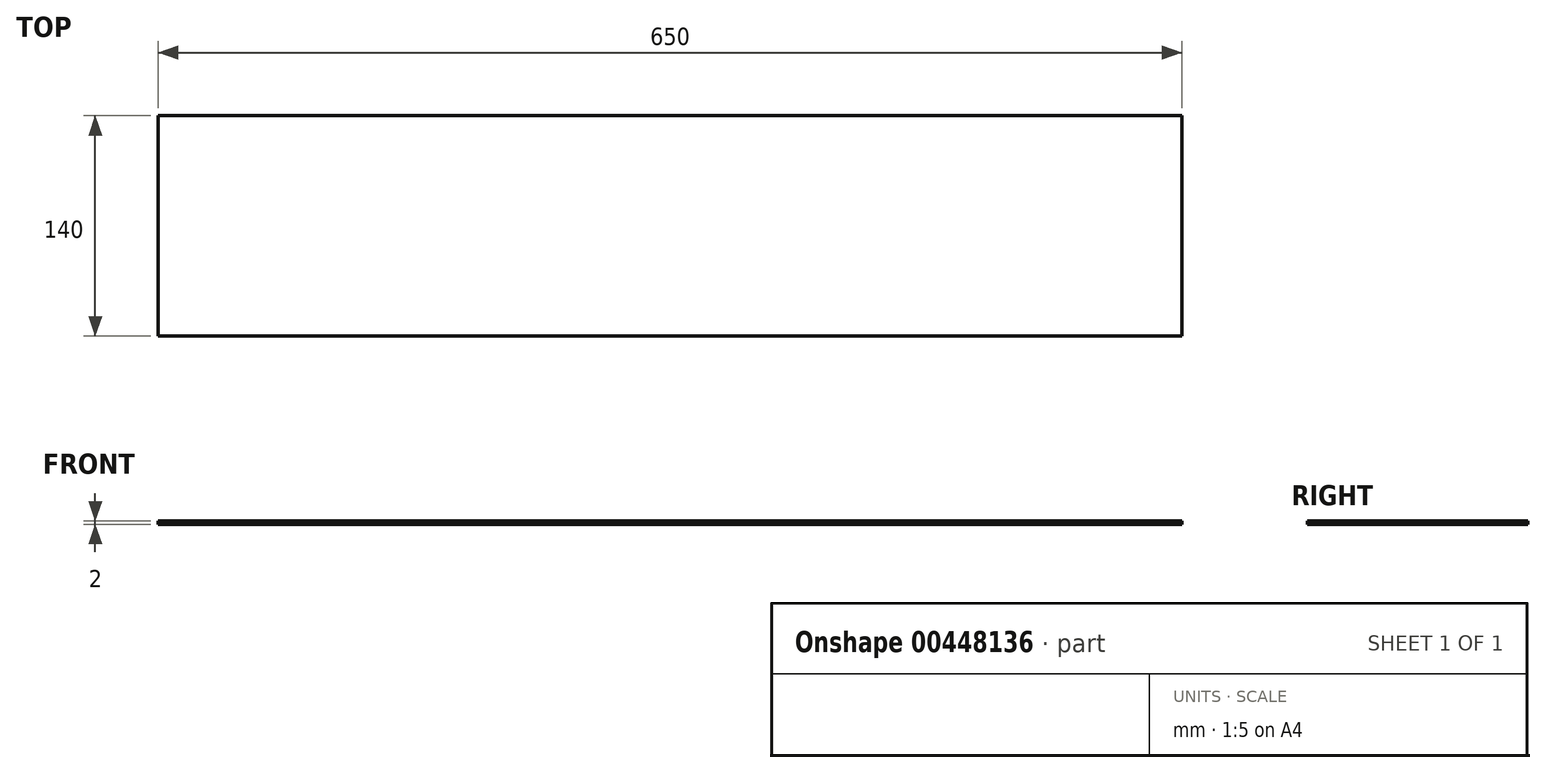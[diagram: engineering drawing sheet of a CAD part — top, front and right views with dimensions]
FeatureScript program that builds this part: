
annotation { "Feature Type Name" : "Feature", "Feature Type Description" : "" }
export const myFeature = defineFeature(function(context is Context, id is Id, definition is map)
    precondition{}
    {
        {
            var Q0;
            Q0=qCreatedBy(makeId("Top.planeOp"),FACE);
            var sketch = newSketch(context, id + "F0", { "sketchPlane" : qUnion([Q0])});
            skLineSegment(sketch, "E0.bottom", {"start": v(325, -70) * mm, "end": v(-325, -70) * mm});
            skLineSegment(sketch, "E0.top", {"start": v(325, 70) * mm, "end": v(-325, 70) * mm});
            skLineSegment(sketch, "E0.left", {"start": v(325, -70) * mm, "end": v(325, 70) * mm});
            skLineSegment(sketch, "E0.right", {"start": v(-325, -70) * mm, "end": v(-325, 70) * mm});
            skPoint(sketch, "E0.middle", {"position": v(0, 0) * mm});
            skSolve(sketch);
        }
        {
            var Q0;
            Q0 = qSketchRegion(id + "F0", true);
            extrude(context, id + "F1", {"entities" : qUnion([Q0]), "flatOperationType" : FlatOperationType.REMOVE, "offsetDistance" : 25.4 * mm, "depth" : 2 * mm, "domain" : OperationDomain.MODEL});
        }
    });
